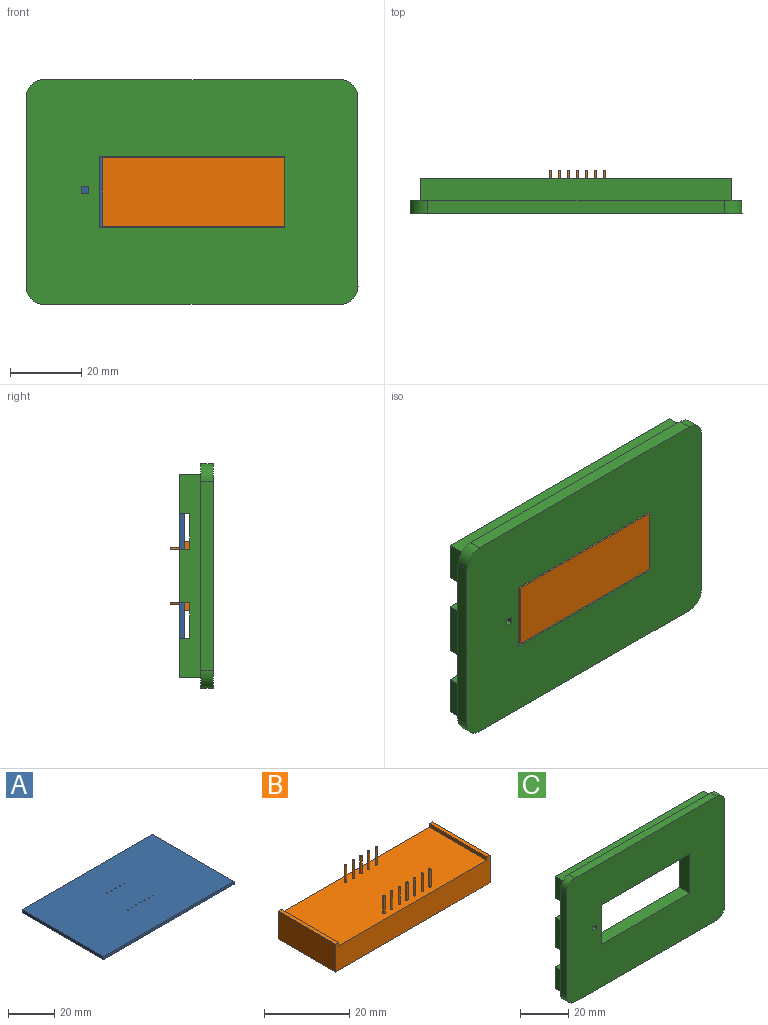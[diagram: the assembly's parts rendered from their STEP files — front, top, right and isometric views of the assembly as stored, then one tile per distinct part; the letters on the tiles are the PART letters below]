
ASSEMBLY  parts=3 mates=2
PART A: 18 faces, bbox 80x50x1.6 mm
  f0: plane 80x1.6mm, normal (0,-1,0), area 128mm2, adj f1,f3,f4,f5
  f1: plane 50x1.6mm, normal (1,0,0), area 80mm2, adj f0,f2,f4,f5
  f2: plane 80x1.6mm, normal (0,1,0), area 128mm2, adj f1,f3,f4,f5
  f3: plane 50x1.6mm, normal (-1,0,0), area 80mm2, adj f0,f2,f4,f5
  f4: plane 80x50mm, normal (0,0,1), area 3997.6mm2, adj f0,f1,f2,f3,f6,f7,f8,f9
  f5: plane 80x50mm, normal (0,0,-1), area 3997.6mm2, adj f0,f1,f2,f3,f6,f7,f8,f9
  f6: cylinder r=0.25mm len=1.6mm, axis (0,0,1), area 2.5mm2, adj f4,f5
  f7: cylinder r=0.25mm len=1.6mm, axis (0,0,1), area 2.5mm2, adj f4,f5
  f8: cylinder r=0.25mm len=1.6mm, axis (0,0,1), area 2.5mm2, adj f4,f5
  f9: cylinder r=0.25mm len=1.6mm, axis (0,0,1), area 2.5mm2, adj f4,f5
  f10: cylinder r=0.25mm len=1.6mm, axis (0,0,1), area 2.5mm2, adj f4,f5
  f11: cylinder r=0.25mm len=1.6mm, axis (0,0,1), area 2.5mm2, adj f4,f5
  f12: cylinder r=0.25mm len=1.6mm, axis (0,0,1), area 2.5mm2, adj f4,f5
  f13: cylinder r=0.25mm len=1.6mm, axis (0,0,1), area 2.5mm2, adj f4,f5
  f14: cylinder r=0.25mm len=1.6mm, axis (0,0,1), area 2.5mm2, adj f4,f5
  f15: cylinder r=0.25mm len=1.6mm, axis (0,0,1), area 2.5mm2, adj f4,f5
  f16: cylinder r=0.25mm len=1.6mm, axis (0,0,1), area 2.5mm2, adj f4,f5
  f17: cylinder r=0.25mm len=1.6mm, axis (0,0,1), area 2.5mm2, adj f4,f5
PART B: 34 faces, bbox 51.2x19.1x12 mm
  f0: plane 49.2x19.1mm, normal (0,0,1), area 937.4mm2, adj f2,f4,f6,f8,f10,f12,f14,f16
  f1: plane 19.1x8mm, normal (-1,0,0), area 152.8mm2, adj f2,f4,f5,f7
  f2: plane 51.2x8mm, normal (0,-1,0), area 360.4mm2, adj f0,f1,f3,f5,f6,f7,f8,f9
  f3: plane 19.1x8mm, normal (1,0,0), area 152.8mm2, adj f2,f4,f5,f9
  f4: plane 51.2x8mm, normal (0,1,0), area 360.4mm2, adj f0,f1,f3,f5,f6,f7,f8,f9
  f5: plane 51.2x19.1mm, normal (0,0,-1), area 977.9mm2, adj f1,f2,f3,f4
  f6: plane 19.1x1mm, normal (1,0,0), area 19.1mm2, adj f0,f2,f4,f7
  f7: plane 19.1x1mm, normal (0,0,1), area 19.1mm2, adj f1,f2,f4,f6
  f8: plane 19.1x1mm, normal (-1,0,0), area 19.1mm2, adj f0,f2,f4,f9
  f9: plane 19.1x1mm, normal (0,0,1), area 19.1mm2, adj f2,f3,f4,f8
  f10: cylinder r=0.25mm len=5mm, axis (0,0,-1), area 7.9mm2, adj f0,f11
  f11: plane 0.5x0.5mm, normal (0,0,1), area 0.2mm2, adj f10
  f12: cylinder r=0.25mm len=5mm, axis (0,0,-1), area 7.9mm2, adj f0,f13
  f13: plane 0.5x0.5mm, normal (0,0,1), area 0.2mm2, adj f12
  f14: cylinder r=0.25mm len=5mm, axis (0,0,-1), area 7.9mm2, adj f0,f15
  f15: plane 0.5x0.5mm, normal (0,0,1), area 0.2mm2, adj f14
  f16: cylinder r=0.25mm len=5mm, axis (0,0,-1), area 7.9mm2, adj f0,f17
  f17: plane 0.5x0.5mm, normal (0,0,1), area 0.2mm2, adj f16
  f18: cylinder r=0.25mm len=5mm, axis (0,0,-1), area 7.9mm2, adj f0,f19
  f19: plane 0.5x0.5mm, normal (0,0,1), area 0.2mm2, adj f18
  f20: cylinder r=0.25mm len=5mm, axis (0,0,-1), area 7.9mm2, adj f0,f21
  f21: plane 0.5x0.5mm, normal (0,0,1), area 0.2mm2, adj f20
  f22: cylinder r=0.25mm len=5mm, axis (0,0,-1), area 7.9mm2, adj f0,f23
  f23: plane 0.5x0.5mm, normal (0,0,1), area 0.2mm2, adj f22
  f24: cylinder r=0.25mm len=5mm, axis (0,0,-1), area 7.9mm2, adj f0,f25
  f25: plane 0.5x0.5mm, normal (0,0,1), area 0.2mm2, adj f24
  f26: cylinder r=0.25mm len=5mm, axis (0,0,-1), area 7.9mm2, adj f0,f27
  f27: plane 0.5x0.5mm, normal (0,0,1), area 0.2mm2, adj f26
  f28: cylinder r=0.25mm len=5mm, axis (0,0,-1), area 7.9mm2, adj f0,f29
  f29: plane 0.5x0.5mm, normal (0,0,1), area 0.2mm2, adj f28
  f30: cylinder r=0.25mm len=5mm, axis (0,0,-1), area 7.9mm2, adj f0,f31
  f31: plane 0.5x0.5mm, normal (0,0,1), area 0.2mm2, adj f30
  f32: cylinder r=0.25mm len=5mm, axis (0,0,-1), area 7.9mm2, adj f0,f33
  f33: plane 0.5x0.5mm, normal (0,0,1), area 0.2mm2, adj f32
PART C: 55 faces, bbox 93x9.6x63 mm
  f0: plane 81x8mm, normal (0,1,0), area 141mm2, adj f7,f9,f24,f27,f28,f29,f46,f54
  f1: plane 15x1.5mm, normal (0,1,0), area 22.5mm2, adj f10,f29,f43,f47
  f2: plane 15x1.5mm, normal (0,1,0), area 22.5mm2, adj f8,f27,f51,f53
  f3: plane 15x3mm, normal (0,1,0), area 45mm2, adj f8,f20,f51,f53
  f4: plane 15x3mm, normal (0,1,0), area 45mm2, adj f6,f10,f43,f47
  f5: plane 87x11mm, normal (0,1,0), area 309mm2, adj f6,f20,f22,f23,f25,f26,f44,f50
  f6: plane 57x6mm, normal (1,0,0), area 282mm2, adj f4,f5,f14,f19,f21,f22,f43,f44
  f7: plane 8x1.6mm, normal (1,0,0), area 12.8mm2, adj f0,f14,f24,f54
  f8: plane 15x1.6mm, normal (1,0,0), area 24mm2, adj f2,f3,f51,f53
  f9: plane 8x1.6mm, normal (-1,0,0), area 12.8mm2, adj f0,f14,f24,f46
  f10: plane 15x1.6mm, normal (-1,0,0), area 24mm2, adj f1,f4,f43,f47
  f11: plane 78x48mm, normal (0,1,0), area 2700mm2, adj f27,f28,f29,f30,f31,f32,f33,f34
  f12: plane 93x63mm, normal (0,-1,0), area 4793.5mm2, adj f15,f16,f17,f18,f31,f32,f33,f34
  f13: plane 81x8mm, normal (0,1,0), area 141mm2, adj f23,f25,f26,f27,f29,f30,f44,f50
  f14: plane 87x11mm, normal (0,1,0), area 309mm2, adj f6,f7,f9,f20,f21,f24,f46,f54
  f15: plane 83x3.6mm, normal (0,0,1), area 298.8mm2, adj f12,f19,f39,f42
  f16: plane 53x3.6mm, normal (-1,0,0), area 190.8mm2, adj f12,f19,f39,f40
  f17: plane 83x3.6mm, normal (0,0,-1), area 298.8mm2, adj f12,f19,f40,f41
  f18: plane 53x3.6mm, normal (1,0,0), area 190.8mm2, adj f12,f19,f41,f42
  f19: plane 93x63mm, normal (0,1,0), area 878.5mm2, adj f6,f15,f16,f17,f18,f20,f21,f22
  f20: plane 57x6mm, normal (-1,0,0), area 282mm2, adj f3,f5,f14,f19,f21,f22,f49,f50
  f21: plane 87x6mm, normal (0,0,1), area 522mm2, adj f6,f14,f19,f20
  f22: plane 87x6mm, normal (0,0,-1), area 522mm2, adj f5,f6,f19,f20
  f23: plane 8x1.6mm, normal (1,0,0), area 12.8mm2, adj f5,f13,f26,f50
  f24: plane 81x1.6mm, normal (0,0,-1), area 129.6mm2, adj f0,f7,f9,f14
  f25: plane 8x1.6mm, normal (-1,0,0), area 12.8mm2, adj f5,f13,f26,f44
  f26: plane 81x1.6mm, normal (0,0,1), area 129.6mm2, adj f5,f13,f23,f25
  f27: plane 48x2mm, normal (1,0,0), area 68mm2, adj f0,f2,f11,f13,f28,f30,f49,f50
  f28: plane 78x2mm, normal (0,0,-1), area 156mm2, adj f0,f11,f27,f29
  f29: plane 48x2mm, normal (-1,0,0), area 68mm2, adj f0,f1,f11,f13,f28,f30,f43,f44
  f30: plane 78x2mm, normal (0,0,1), area 156mm2, adj f11,f13,f27,f29
  f31: plane 6x2mm, normal (0,0,-1), area 12mm2, adj f11,f12,f32,f34
  f32: plane 6x2mm, normal (1,0,0), area 12mm2, adj f11,f12,f31,f33
  f33: plane 6x2mm, normal (0,0,1), area 12mm2, adj f11,f12,f32,f34
  f34: plane 6x2mm, normal (-1,0,0), area 12mm2, adj f11,f12,f31,f33
  f35: plane 52x6mm, normal (0,0,-1), area 312mm2, adj f11,f12,f36,f38
  f36: plane 20x6mm, normal (1,0,0), area 120mm2, adj f11,f12,f35,f37
  f37: plane 52x6mm, normal (0,0,1), area 312mm2, adj f11,f12,f36,f38
  f38: plane 20x6mm, normal (-1,0,0), area 120mm2, adj f11,f12,f35,f37
  f39: cylinder r=5mm len=5mm, axis (0,-1,0), area 28.3mm2, adj f12,f15,f16,f19
  f40: cylinder r=5mm len=5mm, axis (0,1,0), area 28.3mm2, adj f12,f16,f17,f19
  f41: cylinder r=5mm len=5mm, axis (0,-1,0), area 28.3mm2, adj f12,f17,f18,f19
  f42: cylinder r=5mm len=5mm, axis (0,1,0), area 28.3mm2, adj f12,f15,f18,f19
  f43: plane 4.5x3mm, normal (0,0,-1), area 11.1mm2, adj f1,f4,f6,f10,f29,f45
  f44: plane 4.5x3mm, normal (0,0,1), area 11.1mm2, adj f5,f6,f13,f25,f29,f45
  f45: plane 10x4.5mm, normal (0,1,0), area 45mm2, adj f6,f29,f43,f44
  f46: plane 4.5x3mm, normal (0,0,-1), area 11.1mm2, adj f0,f6,f9,f14,f29,f48
  f47: plane 4.5x3mm, normal (0,0,1), area 11.1mm2, adj f1,f4,f6,f10,f29,f48
  f48: plane 10x4.5mm, normal (0,1,0), area 45mm2, adj f6,f29,f46,f47
  f49: plane 10x4.5mm, normal (0,1,0), area 45mm2, adj f20,f27,f50,f51
  f50: plane 4.5x3mm, normal (0,0,1), area 11.1mm2, adj f5,f13,f20,f23,f27,f49
  f51: plane 4.5x3mm, normal (0,0,-1), area 11.1mm2, adj f2,f3,f8,f20,f27,f49
  f52: plane 10x4.5mm, normal (0,1,0), area 45mm2, adj f20,f27,f53,f54
  f53: plane 4.5x3mm, normal (0,0,1), area 11.1mm2, adj f2,f3,f8,f20,f27,f52
  f54: plane 4.5x3mm, normal (0,0,-1), area 11.1mm2, adj f0,f7,f14,f20,f27,f52
PLACE A rot(axis=(-1,0,0),90deg) t=(10.54,-7.07,7.56)mm
PLACE B rot(axis=(-1,0,0),90deg) t=(26.6,-15.07,-15.07)mm
PLACE C rot(axis=(0.58,-0.56,0.59),0deg) t=(11.04,-11.47,7.56)mm
MATE fastened B.f3 <-> C.f38  axis (1,0,0) through (37.04,-11.07,7.56)mm
MATE fastened A.f5 <-> C.f2  axis (0,-1,0) through (-29.46,-7.07,7.56)mm
